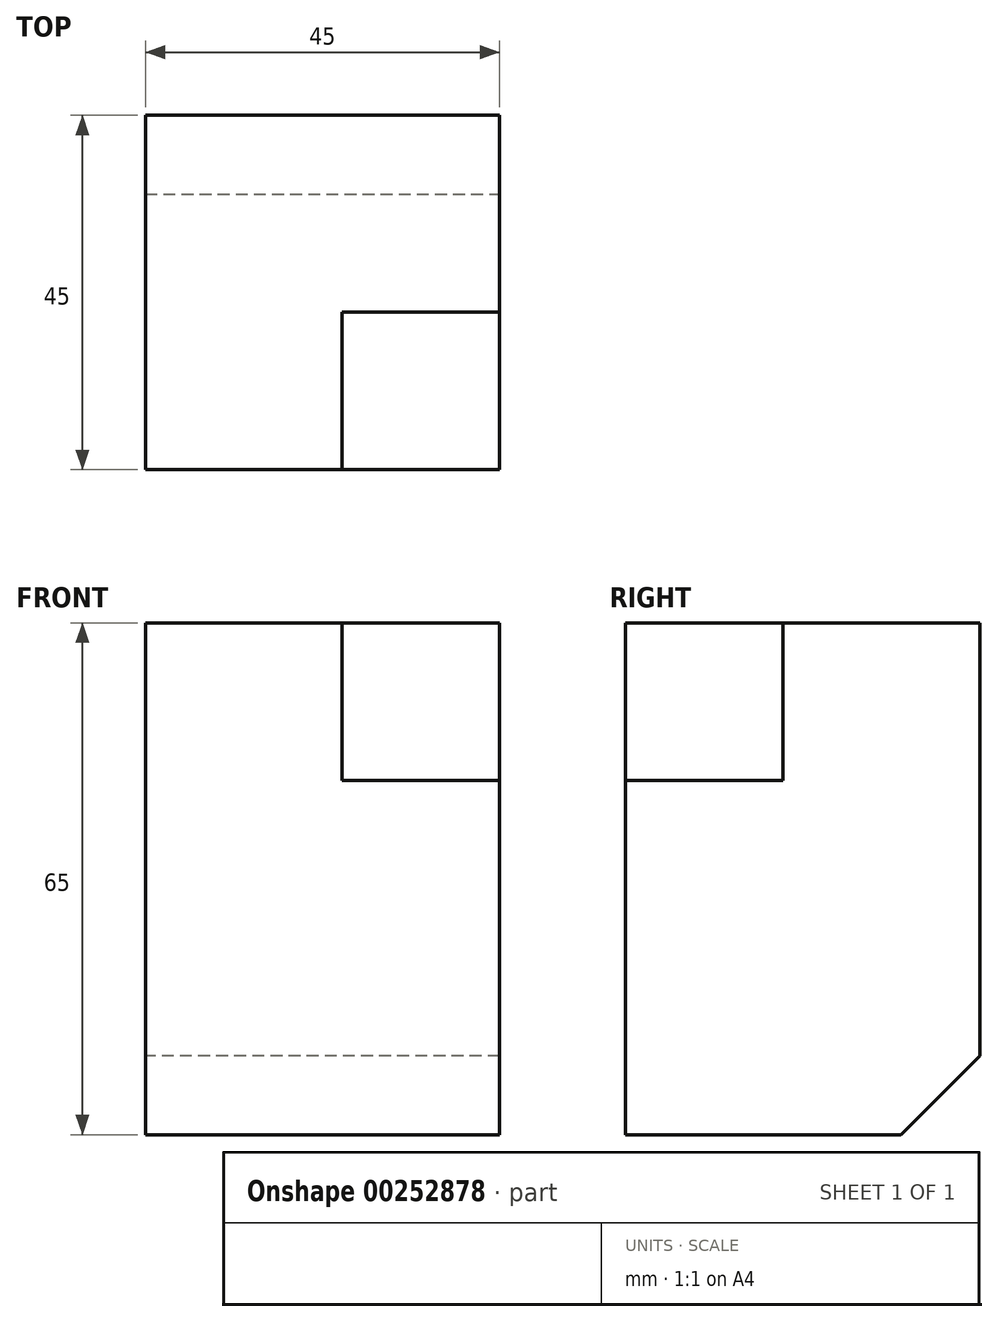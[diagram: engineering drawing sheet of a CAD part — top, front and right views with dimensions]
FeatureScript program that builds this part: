
annotation { "Feature Type Name" : "Feature", "Feature Type Description" : "" }
export const myFeature = defineFeature(function(context is Context, id is Id, definition is map)
    precondition{}
    {
        {
            var Q0;
            Q0=qCreatedBy(makeId("Top.planeOp"),FACE);
            var sketch = newSketch(context, id + "F0", { "sketchPlane" : qUnion([Q0])});
            skLineSegment(sketch, "E0.bottom", {"start": v(0, 0) * mm, "end": v(45, 0) * mm});
            skLineSegment(sketch, "E0.top", {"start": v(0, 45) * mm, "end": v(45, 45) * mm});
            skLineSegment(sketch, "E0.left", {"start": v(0, 0) * mm, "end": v(0, 45) * mm});
            skLineSegment(sketch, "E0.right", {"start": v(45, 0) * mm, "end": v(45, 45) * mm});
            skSolve(sketch);
        }
        {
            var Q0;
            Q0=makeQuery(id+"F0.imprint","IMPRINT",FACE,{"disambiguationData":[TD([[makeQuery(id+"F0.imprint","IMPRINT",EDGE,{"derivedFrom":sQuery(id+"F0.wireOp",EDGE,"E0.bottom")}),1.0]])]});
            extrude(context, id + "F1", {"entities" : qUnion([Q0]), "depth" : 65 * mm});
        }
        {
            var Q0;
            Q0=makeQuery(id+"F1.opExtrude","SWEPT_FACE",FACE,{"disambiguationData":[OSD([sQuery(id+"F0.wireOp",EDGE,"E0.right")])]});
            var sketch = newSketch(context, id + "F2", { "sketchPlane" : qUnion([Q0])});
            skLineSegment(sketch, "E1.bottom", {"start": v(0, 65) * mm, "end": v(20, 65) * mm});
            skLineSegment(sketch, "E1.top", {"start": v(0, 45) * mm, "end": v(20, 45) * mm});
            skLineSegment(sketch, "E1.left", {"start": v(0, 65) * mm, "end": v(0, 45) * mm});
            skLineSegment(sketch, "E1.right", {"start": v(20, 65) * mm, "end": v(20, 45) * mm});
            skSolve(sketch);
        }
        {
            var Q0;
            Q0=makeQuery(id+"F2.imprint","IMPRINT",FACE,{"disambiguationData":[TD([[makeQuery(id+"F2.imprint","IMPRINT",EDGE,{"derivedFrom":sQuery(id+"F2.wireOp",EDGE,"E1.bottom")}),-1.0]])]});
            extrude(context, id + "F3", {"entities" : qUnion([Q0]), "operationType" : NewBodyOperationType.REMOVE, "oppositeDirection" : true, "depth" : 20 * mm});
        }
        {
            var Q0;
            Q0=makeQuery(id+"F1.opExtrude","CAP_EDGE",EDGE,{"disambiguationData":[OSD([sQuery(id+"F0.wireOp",EDGE,"E0.top")])],"isStart":true});
            chamfer(context, id + "F4", {"entities" : qUnion([Q0]), "width" : 10 * mm, "tangentPropagation" : true});
        }
    });
